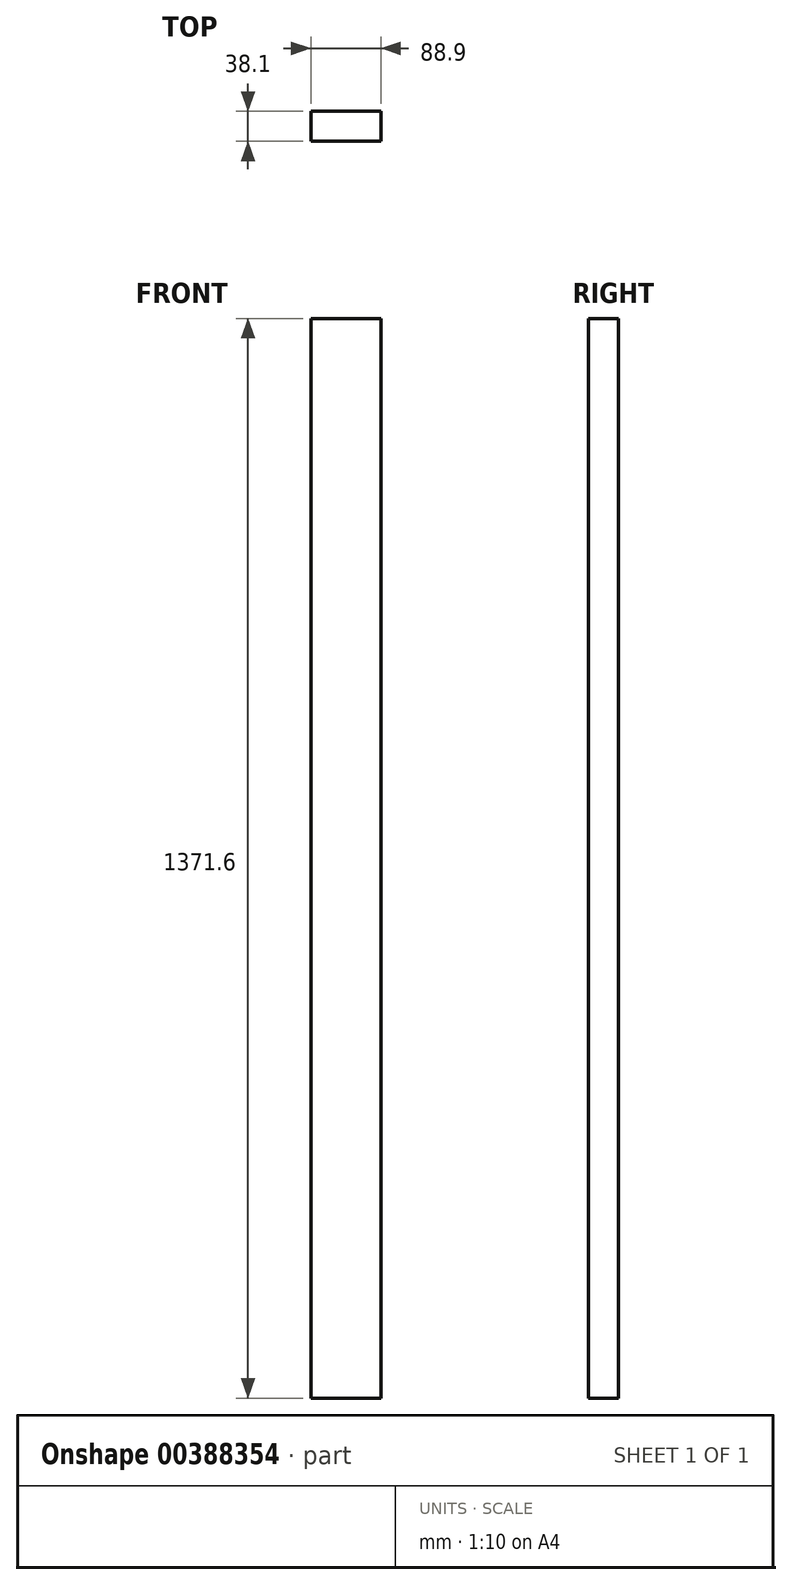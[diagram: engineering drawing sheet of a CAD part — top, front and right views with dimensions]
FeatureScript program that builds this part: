
annotation { "Feature Type Name" : "Feature", "Feature Type Description" : "" }
export const myFeature = defineFeature(function(context is Context, id is Id, definition is map)
    precondition{}
    {
        {
            var Q0;
            Q0=qCreatedBy(makeId("Top.planeOp"),FACE);
            var sketch = newSketch(context, id + "F0", { "sketchPlane" : qUnion([Q0])});
            skLineSegment(sketch, "E0.bottom", {"start": v(44.45, -19.05) * mm, "end": v(-44.45, -19.05) * mm});
            skLineSegment(sketch, "E0.top", {"start": v(44.45, 19.05) * mm, "end": v(-44.45, 19.05) * mm});
            skLineSegment(sketch, "E0.left", {"start": v(44.45, -19.05) * mm, "end": v(44.45, 19.05) * mm});
            skLineSegment(sketch, "E0.right", {"start": v(-44.45, -19.05) * mm, "end": v(-44.45, 19.05) * mm});
            skPoint(sketch, "E0.middle", {"position": v(0, 0) * mm});
            skSolve(sketch);
        }
        {
            var Q0;
            Q0=makeQuery(id+"F0.imprint","IMPRINT",FACE,{"disambiguationData":[TD([[makeQuery(id+"F0.imprint","IMPRINT",EDGE,{"derivedFrom":sQuery(id+"F0.wireOp",EDGE,"E0.bottom")}),-1.0]])]});
            extrude(context, id + "F1", {"entities" : qUnion([Q0]), "depth" : 1371.6 * mm});
        }
    });
